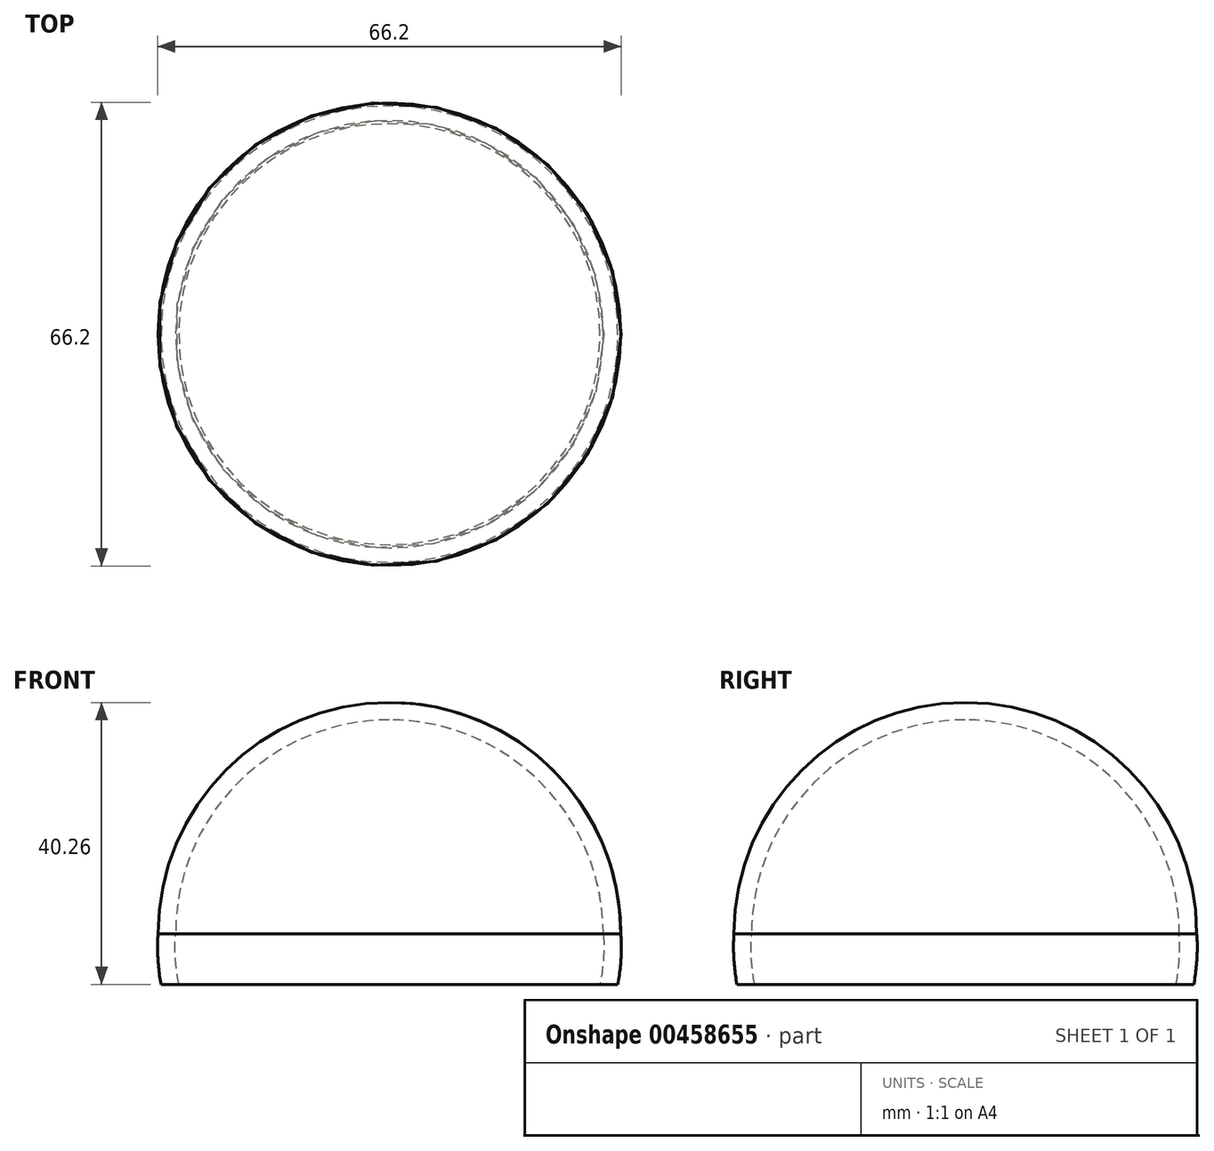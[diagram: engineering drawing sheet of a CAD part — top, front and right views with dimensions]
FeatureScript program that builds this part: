
annotation { "Feature Type Name" : "Feature", "Feature Type Description" : "" }
export const myFeature = defineFeature(function(context is Context, id is Id, definition is map)
    precondition{}
    {
        {
            var Q0;
            Q0=qCreatedBy(makeId("Front.planeOp"),FACE);
            var sketch = newSketch(context, id + "F0", { "sketchPlane" : qUnion([Q0])});
            skCircle(sketch, "E0", {"center": v(0, 64.17) * mm, "radius": 33.02 * mm});
            skLineSegment(sketch, "E1.bottom", {"start": v(13.08, -36.16) * mm, "end": v(-13.08, -36.16) * mm});
            skLineSegment(sketch, "E1.top", {"start": v(13.08, -9.49) * mm, "end": v(-13.08, -9.49) * mm});
            skLineSegment(sketch, "E1.left", {"start": v(13.08, -36.16) * mm, "end": v(13.08, -9.49) * mm});
            skLineSegment(sketch, "E1.right", {"start": v(-13.08, -36.16) * mm, "end": v(-13.08, -9.49) * mm});
            skPoint(sketch, "E1.middle", {"position": v(0, -22.82) * mm});
            skFitSpline(sketch, "E2", {"points": [v(-33.02, 64.17) * mm, v(-13.08, -9.49) * mm], "startDerivative": vector(-4.54, -55.65) * mm, "endDerivative": vector(0, -88.84) * mm});
            skFitSpline(sketch, "E3.MirrorCS", {"points": [v(33.02, 64.17) * mm, v(13.08, -9.49) * mm], "startDerivative": vector(4.54, -55.65) * mm, "endDerivative": vector(0, -88.84) * mm});
            skLineSegment(sketch, "E4", {"start": v(0, 97.2) * mm, "end": v(0, -36.16) * mm});
            skLineSegment(sketch, "E5", {"start": v(-32.6, 56.93) * mm, "end": v(32.6, 56.93) * mm});
            skLineSegment(sketch, "E6", {"start": v(-13.08, -28.16) * mm, "end": v(13.08, -28.16) * mm});
            skLineSegment(sketch, "E7", {"start": v(-13.08, -28.16) * mm, "end": v(-8, -36.16) * mm});
            skLineSegment(sketch, "E8", {"start": v(13.08, -28.16) * mm, "end": v(8, -36.16) * mm});
            skSolve(sketch);
        }
        {
            var Q0;
            {var subQ0=sQuery(id+"F0.wireOp",EDGE,"E0");var subQ1=makeQuery(id+"F0.imprint","INTERSECT",VERTEX,{"derivedFrom":[subQ0,sQuery(id+"F0.wireOp",EDGE,"E3.MirrorCS")]});Q0=makeQuery(id+"F0.imprint","IMPRINT",FACE,{"disambiguationData":[TD([[makeQuery(id+"F0.imprint","IMPRINT",EDGE,{"disambiguationData":[TD([[subQ1,-1.0]])],"derivedFrom":subQ0}),1.0]])]});}
            var Q1;
            {var subQ0=sQuery(id+"F0.wireOp",EDGE,"E3.MirrorCS");var subQ1=sQuery(id+"F0.wireOp",EDGE,"E0");var subQ2=makeQuery(id+"F0.imprint","INTERSECT",VERTEX,{"derivedFrom":[subQ1,subQ0]});Q1=makeQuery(id+"F0.imprint","IMPRINT",FACE,{"disambiguationData":[TD([[makeQuery(id+"F0.imprint","IMPRINT",EDGE,{"disambiguationData":[TD([[subQ2,1.0]])],"derivedFrom":subQ1}),-1.0]])]});}
            var Q2;
            Q2=sQuery(id+"F0.wireOp",EDGE,"E4");
            revolve(context, id + "F1", {"entities" : qUnion([Q0, Q1]), "axis" : qUnion([Q2]), "revolveType" : RevolveType.FULL});
        }
        {
            var Q0;
            Q0=makeQuery(id+"F1.opRevolve","SWEPT_FACE",FACE,{"disambiguationData":[OSD([sQuery(id+"F0.wireOp",EDGE,"E5")])]});
            shell(context, id + "F2", {"entities" : qUnion([Q0]), "thickness" : 2.5 * mm});
        }
    });
